# Revit family: Rohrschellen Form A, Titan HD, o.D.
name_source: partatom
category: HLS-Bauteile
revit_build: Autodesk Revit 2017 (Build: 20190507_1515(x64)
units: mm (PartAtom-declared; Revit-internal decimal feet)

## family parameters
Arbeitsebenenbasiert = Ja
Beim Laden mit Abzugskörper schneiden = Nein
Bemaßung runder Anschluss = Durchmesser verwenden
Gemeinsam genutzt = Ja
Immer vertikal = Nein
Raumberechnungspunkt = Nein
Teiletyp = Normal

## types (18) — shared parameters
A = 5 mm  [stored 0.0164042 ft]
Anschluss = ohne Anschluss
Bauart = zweiteilig
C = 17 mm
DF1 = 34 mm
DF2 = 17 mm
DVS = 13 mm
Fabrikat = MEFA
Firma = MEFA Befestigungs- und Montagesysteme GmbH
Kurztext1 = Rohrschelle Form A Titan HD 50x5,0
MB = 50 mm  [stored 0.164042 ft]
MD = 5 mm  [stored 0.0164042 ft]
Material = Stahl
Materialmaße = 50x5,0 mm
Mengeneinheit = St
Oberflaeche = galvanisch verzinkt
Rohraußendurchmesser Zoll = Zoll
Verschluss-Schraube = M12
Vorgabe-Ansicht = 1219 mm
max. zul. Last horizontal = 0.00 kN
max. zul. Last vertikal = 0.00 kN
vpe = 1 St
zero-valued in all types: HGA, Nennweite DN Rohr, Stärke Material, max. Rohraußendurchmesser, min. Rohraußendurchmesser

## per-type parameters (varying)
| type | AB | Achsabstand | Artikelnummer | B | D | EAN | Gewicht | Gewicht pro Bauteil | H | Kurztext2 | R | RM | Rohraußendurchmesser | S |
| Rohrschellen Form A, Ø108, o.D. | 0 mm  [stored 0 ft] | 148 mm | 0070512 | 182 mm | 108 mm | 4250928402837 | 0.89 kg | 0.89 kg | 118 mm | 108 mm ohne Anschluss | 54 mm | 59 mm | 108 mm | 148 mm |
| Rohrschellen Form A, Ø110, o.D. | 0 mm  [stored 0 ft] | 148 mm | 0070512 | 184 mm | 110 mm | 4250928402837 | 0.89 kg | 0.89 kg | 120 mm | 108 mm ohne Anschluss | 55 mm | 60 mm | 108 mm | 150 mm |
| Rohrschellen Form A, Ø114, o.D. | 0 mm  [stored 0 ft] | 148 mm | 0070514 | 188 mm | 114 mm  [stored 0.374016 ft] | 4250928402837 | 0.89 kg | 0.89 kg | 124 mm | 108 mm ohne Anschluss | 57 mm  [stored 0.187008 ft] | 62 mm  [stored 0.203412 ft] | 108 mm | 154 mm |
| Rohrschellen Form A, Ø133, o.D. | 0 mm  [stored 0 ft] | 173 mm | 0070581 | 207 mm | 133 mm | 4250928402899 | 1.05 kg | 1.05 kg | 143 mm | 133 mm ohne Anschluss | 67 mm | 72 mm | 133 mm | 173 mm |
| Rohrschellen Form A, Ø135, o.D. | 0 mm  [stored 0 ft] | 173 mm | 0070581 | 209 mm | 135 mm | 4250928402899 | 1.05 kg | 1.05 kg | 145 mm | 133 mm ohne Anschluss | 68 mm | 73 mm | 133 mm | 175 mm |
| Rohrschellen Form A, Ø140, o.D. | 5 mm  [stored 0.0164042 ft] | 180 mm | 0070603 | 214 mm | 140 mm | 4250928402929 | 1.09 kg | 1.09 kg | 150 mm | 140 mm ohne Anschluss | 70 mm  [stored 0.229659 ft] | 75 mm | 140 mm | 180 mm |
| Rohrschellen Form A, Ø159, o.D. | 0 mm  [stored 0 ft] | 200 mm | 0070647 | 233 mm | 159 mm | 4250928402950 | 1.21 kg | 1.21 kg | 169 mm | 159 mm ohne Anschluss | 80 mm  [stored 0.262467 ft] | 85 mm | 159 mm | 199 mm |
| Rohrschellen Form A, Ø165, o.D. | 0 mm  [stored 0 ft] | 205 mm | 0070686 | 239 mm | 165 mm | 4250928402974 | 1.25 kg | 1.25 kg | 175 mm | 165 mm ohne Anschluss | 83 mm | 88 mm | 165 mm | 205 mm |
| Rohrschellen Form A, Ø168, o.D. | 0 mm  [stored 0 ft] | 208 mm | 0070689 | 242 mm | 168 mm | 4250928402981 | 1.27 kg | 1.27 kg | 178 mm | 168 mm ohne Anschluss | 84 mm | 89 mm | 168 mm | 208 mm |
| Rohrschellen Form A, Ø194, o.D. | 0 mm  [stored 0 ft] | 234 mm | 0070751 | 268 mm | 194 mm | 4250928403018 | 1.44 kg | 1.44 kg | 204 mm | 164 mm ohne Anschluss | 97 mm  [stored 0.318241 ft] | 102 mm | 164 mm | 234 mm |
| Rohrschellen Form A, Ø200, o.D. | 0 mm  [stored 0 ft] | 240 mm | 0070778 | 274 mm | 200 mm | 4250928403032 | 1.47 kg | 1.47 kg | 210 mm | 200 mm ohne Anschluss | 100 mm  [stored 0.328084 ft] | 105 mm | 200 mm | 240 mm |
| Rohrschellen Form A, Ø210, o.D. | 0 mm  [stored 0 ft] | 250 mm | 0070786 | 274 mm | 200 mm | 4250928403056 | 1.54 kg | 1.54 kg | 210 mm | 210 mm ohne Anschluss | 100 mm  [stored 0.328084 ft] | 105 mm | 210 mm | 240 mm |
| Rohrschellen Form A, Ø219, o.D. | 0 mm  [stored 0 ft] | 260 mm | 0070808 | 293 mm | 219 mm | 4250928403070 | 1.59 kg | 1.59 kg | 229 mm | 219 mm ohne Anschluss | 110 mm | 115 mm | 219 mm | 259 mm |
| Rohrschellen Form A, Ø267, o.D. | 0 mm  [stored 0 ft] | 307 mm | 0070881 | 341 mm | 267 mm | 4250928403094 | 1.90 kg | 1.90 kg | 277 mm | 267 mm ohne Anschluss | 134 mm | 139 mm | 267 mm | 307 mm |
| Rohrschellen Form A, Ø273, o.D. | 0 mm  [stored 0 ft] | 314 mm | 0070891 | 347 mm | 273 mm | 4250928403117 | 1.94 kg | 1.94 kg | 283 mm | 273 mm ohne Anschluss | 137 mm | 142 mm | 273 mm | 313 mm |
| Rohrschellen Form A, Ø324, o.D. | 0 mm  [stored 0 ft] | 364 mm | 0070945 | 398 mm | 324 mm | 4250928403131 | 2.26 kg | 2.26 kg | 334 mm | 324 mm ohne Anschluss | 162 mm | 167 mm | 324 mm | 364 mm |
| Rohrschellen Form A, Ø356, o.D. | 0 mm  [stored 0 ft] | 396 mm | 0070962 | 430 mm | 356 mm | 4250928403155 | 2.47 kg | 2.47 kg | 366 mm | 365 mm ohne Anschluss | 178 mm | 183 mm | 365 mm | 396 mm |
| Rohrschellen Form A, Ø368, o.D. | 0 mm  [stored 0 ft] | 408 mm | 0070964 | 442 mm | 368 mm | 4250928403179 | 2.54 kg | 2.54 kg | 378 mm | 368 mm ohne Anschluss | 184 mm | 189 mm | 368 mm | 408 mm |

note: [stored X ft] marks values corroborated as IEEE doubles in the binary element streams (Revit-internal decimal feet)
